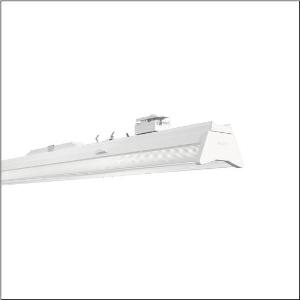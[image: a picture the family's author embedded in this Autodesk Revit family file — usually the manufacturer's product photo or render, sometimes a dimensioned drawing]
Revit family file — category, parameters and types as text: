
# Revit family: licross_r__11_performance_mo_51tm16mn4axg_6102
name_source: partatom
category: Lighting Fixtures
units: mm (PartAtom-declared; Revit-internal decimal feet)

## family parameters
Cut with Voids When Loaded = No
Host = Face
Light Source = No
Part Type = Normal
Room Calculation Point = No
Round Connector Dimension = Use Diameter
Shared = No

## types (1)
- --- (1 x LED, 10160 lm, 55.3 W, 4000K)
    Apparent Load = 55 VA
    CIE Flux Codes = 66 88 96 79 100
    Color Rendering = 80
    Color Temperature = 4000K
    Default Elevation = 1800 mm
    Description = Licross® 11 Performance MO, luminaire insert, of sheet steel, galvanised, coil coated, white, length: 1.500mm, width: 120mm, height: 123mm, LED rated luminous flux: 10.160lm, light colour: 840, control gear: ON/OFF Multilumen, with plug, 3-pole, with phase selection, mains connection: 220..240V, AC, 50/60Hz, rated input power: 55W, halogen-free wiring, primary light control with lens, of plastic, primary optical cover: cover, of PMMA, light emission: direct/indirect distribution, primary light characteristic: symmetric, protection rating (complete): IP40, insulation class (complete): insulation class I (protective earthing), certification: CE, ENEC, VDE, UKCA, protection symbol: D if used in an environment without relevant dust loads with corresponding accessories, impact resistance: IK06, permissible ambient temperature for indoor applications: -35..+40°C, corresponds to IFS (International Featured Standards) requirements for safety and quality in the food industry, reducing of maximum allowable ambient temperature of 5°C with ceiling mounting, LABS conformity tested according to VDMA 24364:2018-05, packaging unit: 1 piece
    Height = 114 mm
    Lamp = 1 x LED
    Lamp Light Flux = 10160 lm
    Lamp Power = 55.3 W
    Lamp count = 1
    Length = 1500 mm
    Luminous efficacy = 184 lm/W
    Manufacturer = Siteco
    ModVariant = No
    Model = 51TM16MN4AXG
    Mounting Place = Ceiling
    Mounting Type = Pendant
    Number of Poles = 1
    OnlyDefault = Yes
    Power Factor = 1
    Product Name = Licross® 11 Performance MO
    Product group = luminaire insert
    ProductGroupID = 901
    Protection Class = Protection class I
    Protection Degree = IP 40
    RLX_Detail_Level = 1
    RLX_Emergency_Light_Flux = 0 lm
    RLX_Emergency_Type = 0
    RLX_Emergency_Type_DB = No
    RlxData = <blob elided: 31829 chars, md5=8f8dd722>
    Socket = socket
    Standby Power = 0 W
    System Light Flux = 10160 lm
    System Power = 55 W
    Type Comments = factory setting: luminous flux: 100 % | (A | C | E) | 126 mA
    Type Image = l_1256138.jpg
    URL = http://relux.com
    VarID = @adj_055485
    Voltage = 0 V
    Weight = 0.00 kg
    Width = 120 mm

## geometry (parser evidence)
native form markers: Blend x4, Sweep x13
no freeform markers — native parametric forms only
